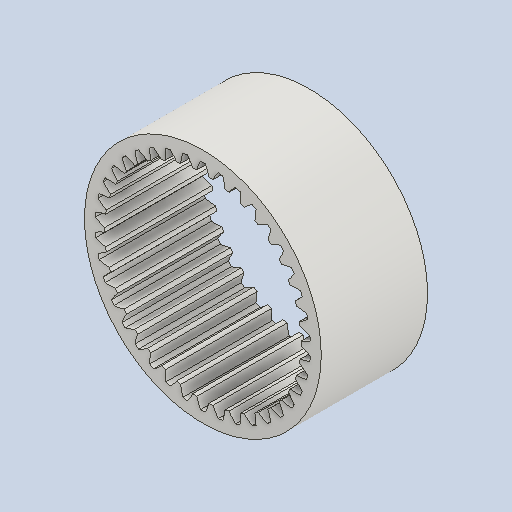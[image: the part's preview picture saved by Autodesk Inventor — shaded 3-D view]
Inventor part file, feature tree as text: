
AUTODESK INVENTOR PART (.ipt)
format: ipt  version: 2024 (Build 280153000, 153)  size: 331,776 bytes
history: native  units: mm (DEFAULTED — no unit token found)
features: plane x3, other x3, extrude x1, sketch x1
ambient origin geometry x8: Origin, YZ Plane, XZ Plane, XY Plane, X Axis, Y Axis, Z Axis, Center Point
bodies: Solid1 (feature_tree)
feature tree (8):
  extrude  "Extrusion1"  Depth=40.0mm TaperAngle=0.0deg
  plane  "Work Plane2"
  plane  "Work Plane8"
  plane  "Work Plane9"
  other  "Spur Gear"
  sketch  "Sketch1"  dims[d0=89.1mm d1=40.0mm d2=0.0mm d3=76.0mm d4=10.0mm d5=0.0mm d16=28.0mm d17=0.0mm d34=0.826735mm d39=0.0mm d45=0.0mm d47=28.0mm d50=0.0mm d51=0.0mm d52=28.0mm]
  other  "Srf1"
  other  "Pitch Diameter"
